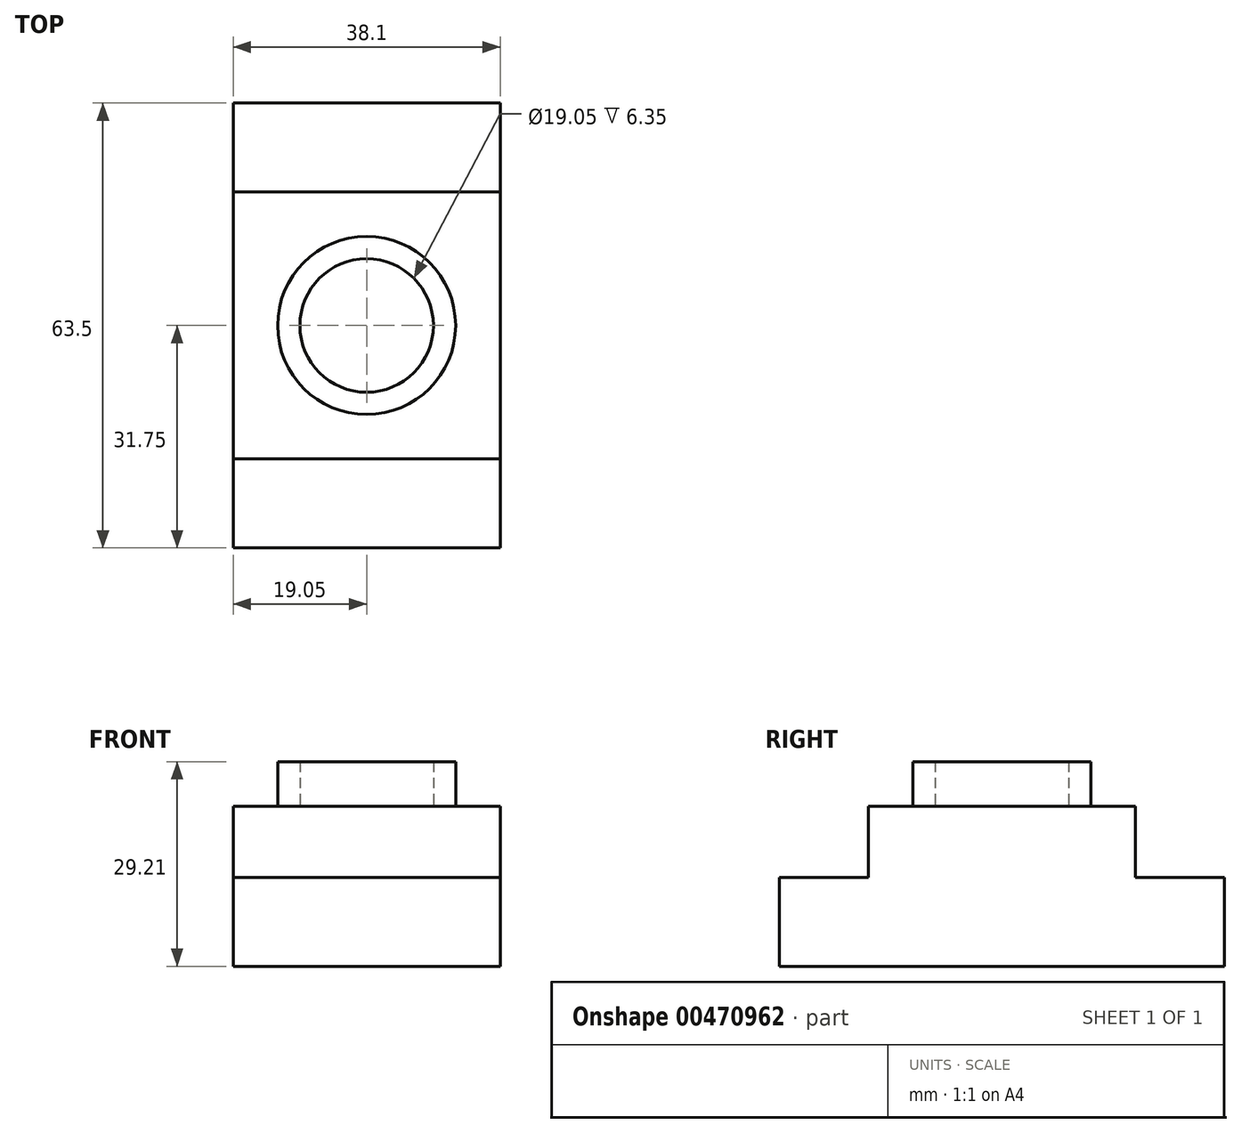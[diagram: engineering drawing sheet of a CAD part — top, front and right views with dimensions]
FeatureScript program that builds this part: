
annotation { "Feature Type Name" : "Feature", "Feature Type Description" : "" }
export const myFeature = defineFeature(function(context is Context, id is Id, definition is map)
    precondition{}
    {
        {
            var Q0;
            Q0=qCreatedBy(makeId("Right.planeOp"),FACE);
            var sketch = newSketch(context, id + "F0", { "sketchPlane" : qUnion([Q0])});
            skLineSegment(sketch, "E0", {"start": v(0, 0) * mm, "end": v(-31.75, 0) * mm});
            skLineSegment(sketch, "E1", {"start": v(-31.75, 0) * mm, "end": v(-31.75, 12.7) * mm});
            skLineSegment(sketch, "E2", {"start": v(-31.75, 12.7) * mm, "end": v(-19.05, 12.7) * mm});
            skLineSegment(sketch, "E3", {"start": v(-19.05, 12.7) * mm, "end": v(-19.05, 22.86) * mm});
            skLineSegment(sketch, "E4", {"start": v(-19.05, 22.86) * mm, "end": v(19.05, 22.86) * mm});
            skLineSegment(sketch, "E5", {"start": v(19.05, 22.86) * mm, "end": v(19.05, 12.7) * mm});
            skLineSegment(sketch, "E6", {"start": v(19.05, 12.7) * mm, "end": v(31.75, 12.7) * mm});
            skLineSegment(sketch, "E7", {"start": v(31.75, 12.7) * mm, "end": v(31.75, 0) * mm});
            skLineSegment(sketch, "E8", {"start": v(31.75, 0) * mm, "end": v(0, 0) * mm});
            skSolve(sketch);
        }
        {
            var Q0;
            Q0 = qSketchRegion(id + "F0", true);
            extrude(context, id + "F1", {"entities" : qUnion([Q0]), "depth" : 38.1 * mm});
        }
        {
            var Q0;
            Q0=makeQuery(id+"F1.opExtrude","SWEPT_FACE",FACE,{"disambiguationData":[OSD([sQuery(id+"F0.wireOp",EDGE,"E4")])]});
            var sketch = newSketch(context, id + "F2", { "sketchPlane" : qUnion([Q0])});
            skCircle(sketch, "E9", {"center": v(19.05, 0) * mm, "radius": 12.7 * mm});
            skPoint(sketch, "E9.centerSnap0", {"position": v(19.05, -19.05) * mm});
            skCircle(sketch, "E10", {"center": v(19.05, 0) * mm, "radius": 9.53 * mm});
            skSolve(sketch);
        }
        {
            var Q0;
            Q0 = qSketchRegion(id + "F2", true);
            extrude(context, id + "F3", {"entities" : qUnion([Q0]), "operationType" : NewBodyOperationType.ADD, "depth" : 6.35 * mm});
        }
    });
